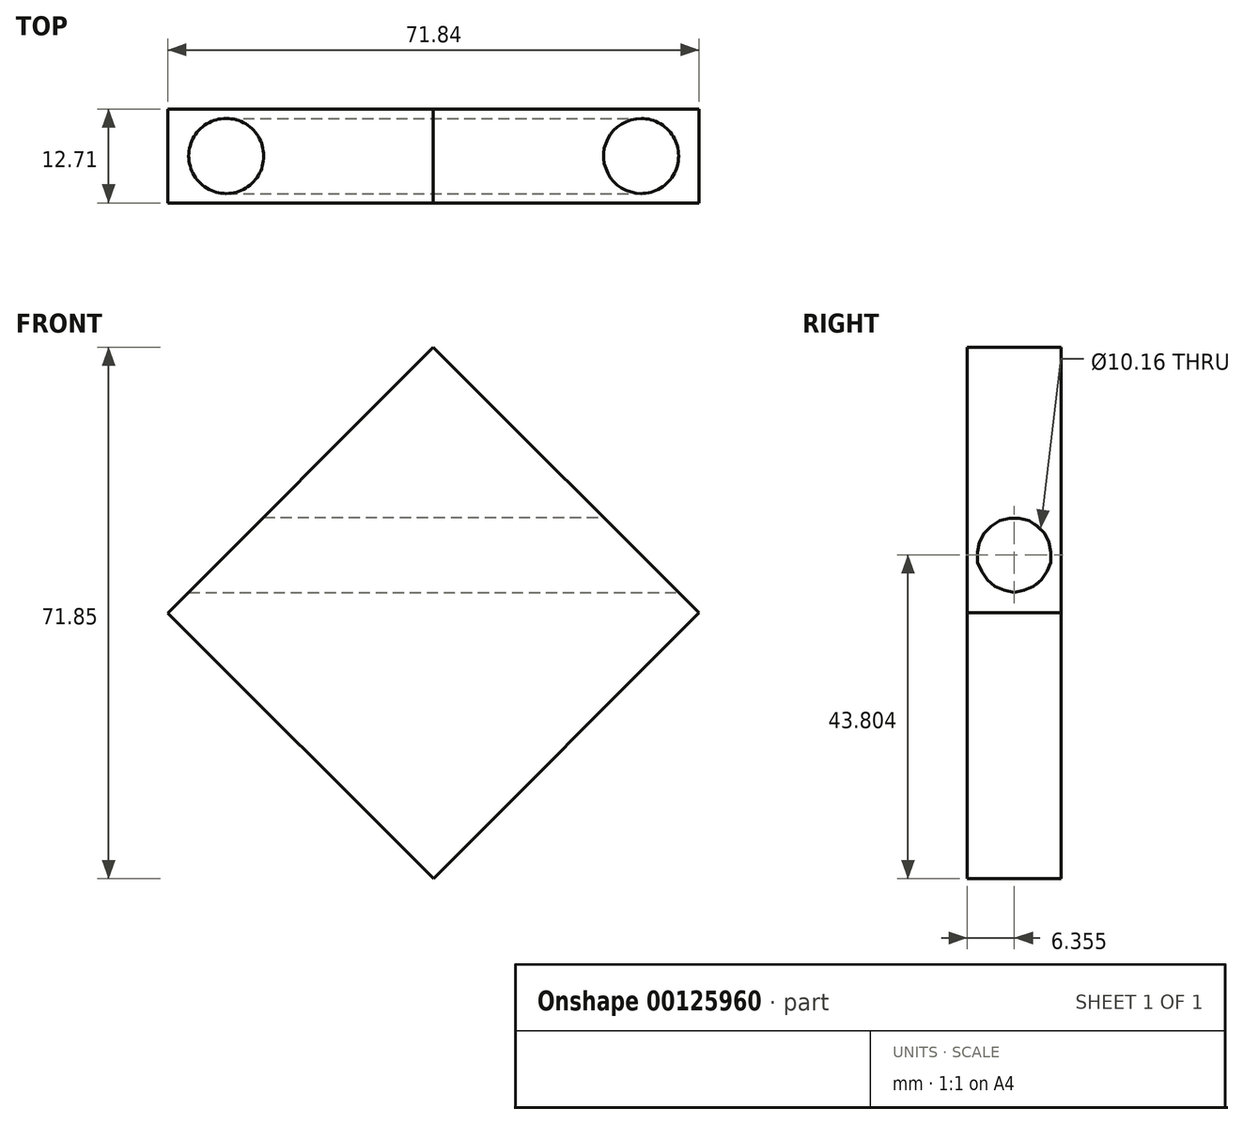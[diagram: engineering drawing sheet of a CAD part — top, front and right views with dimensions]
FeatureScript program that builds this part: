
annotation { "Feature Type Name" : "Feature", "Feature Type Description" : "" }
export const myFeature = defineFeature(function(context is Context, id is Id, definition is map)
    precondition{}
    {
        {
            var Q0;
            Q0=qCreatedBy(makeId("Front.planeOp"),FACE);
            var sketch = newSketch(context, id + "F0", { "sketchPlane" : qUnion([Q0])});
            skLineSegment(sketch, "E0.bottom", {"start": v(-99.41, 44.45) * mm, "end": v(103.79, 44.45) * mm});
            skLineSegment(sketch, "E0.top", {"start": v(-99.41, 0) * mm, "end": v(103.79, 0) * mm});
            skLineSegment(sketch, "E0.left", {"start": v(-99.41, 44.45) * mm, "end": v(-99.41, 0) * mm});
            skLineSegment(sketch, "E0.right", {"start": v(103.79, 44.45) * mm, "end": v(103.79, 0) * mm});
            skSolve(sketch);
        }
        {
            var Q0;
            Q0 = qSketchRegion(id + "F0", true);
            extrude(context, id + "F1", {"entities" : qUnion([Q0]), "endBound" : BoundingType.SYMMETRIC, "depth" : 6.35 * mm});
        }
        {
            var Q0;
            Q0=makeQuery(id+"F1.opExtrude","CAP_FACE",FACE,{"disambiguationData":[OSD([sQuery(id+"F0.wireOp",EDGE,"E0.bottom"),sQuery(id+"F0.wireOp",EDGE,"E0.top"),sQuery(id+"F0.wireOp",EDGE,"E0.left"),sQuery(id+"F0.wireOp",EDGE,"E0.right")])],"isStart":false});
            var sketch = newSketch(context, id + "F2", { "sketchPlane" : qUnion([Q0])});
            skLineSegment(sketch, "E1.bottom", {"start": v(38.1, 22.25) * mm, "end": v(2.16, 58.15) * mm});
            skLineSegment(sketch, "E1.top", {"start": v(2.21, -13.7) * mm, "end": v(-33.73, 22.2) * mm});
            skLineSegment(sketch, "E1.left", {"start": v(38.1, 22.25) * mm, "end": v(2.21, -13.7) * mm});
            skLineSegment(sketch, "E1.right", {"start": v(2.16, 58.15) * mm, "end": v(-33.73, 22.2) * mm});
            skPoint(sketch, "E1.middle", {"position": v(2.19, 22.23) * mm});
            skSolve(sketch);
        }
        {
            var Q0;
            Q0 = qSketchRegion(id + "F2", true);
            extrude(context, id + "F3", {"entities" : qUnion([Q0]), "operationType" : NewBodyOperationType.ADD, "endBound" : BoundingType.SYMMETRIC, "depth" : 12.7 * mm});
        }
        {
            var Q0;
            Q0=makeQuery(id+"F1.opExtrude","SWEPT_BODY",BODY,{"disambiguationData":[OSD([sQuery(id+"F0.wireOp",EDGE,"E0.bottom"),sQuery(id+"F0.wireOp",EDGE,"E0.top"),sQuery(id+"F0.wireOp",EDGE,"E0.left"),sQuery(id+"F0.wireOp",EDGE,"E0.right")])]});
            transform(context, id + "F4", {"entities" : qUnion([Q0]), "transformType" : TransformType.TRANSLATION_3D, "dx" : -2.2 * mm, "dy" : 0 * mm, "dz" : 0 * mm, "makeCopy" : false});
        }
        {
            var Q0;
            {var subQ0=sQuery(id+"F0.wireOp",EDGE,"E0.left");var subQ1=sQuery(id+"F0.wireOp",EDGE,"E0.top");var subQ2=sQuery(id+"F0.wireOp",EDGE,"E0.bottom");Q0=makeQuery(id+"F3.boolean.opBoolean","SPLIT",FACE,{"disambiguationData":[TD([makeQuery(id+"F1.opExtrude","SWEPT_FACE",FACE,{"disambiguationData":[OSD([subQ0])]})])],"derivedFrom":makeQuery(id+"F1.opExtrude","CAP_FACE",FACE,{"disambiguationData":[OSD([subQ2,subQ1,subQ0,sQuery(id+"F0.wireOp",EDGE,"E0.right")])],"isStart":false})});}
            extrude(context, id + "F5", {"entities" : qUnion([Q0]), "operationType" : NewBodyOperationType.REMOVE, "oppositeDirection" : true, "depth" : 25.4 * mm});
        }
        {
            var Q0;
            {var subQ0=sQuery(id+"F0.wireOp",EDGE,"E0.right");var subQ1=sQuery(id+"F0.wireOp",EDGE,"E0.top");var subQ2=sQuery(id+"F0.wireOp",EDGE,"E0.bottom");Q0=makeQuery(id+"F3.boolean.opBoolean","SPLIT",FACE,{"disambiguationData":[TD([makeQuery(id+"F1.opExtrude","SWEPT_FACE",FACE,{"disambiguationData":[OSD([subQ0])]})])],"derivedFrom":makeQuery(id+"F1.opExtrude","CAP_FACE",FACE,{"disambiguationData":[OSD([subQ2,subQ1,sQuery(id+"F0.wireOp",EDGE,"E0.left"),subQ0])],"isStart":false})});}
            extrude(context, id + "F6", {"entities" : qUnion([Q0]), "operationType" : NewBodyOperationType.REMOVE, "oppositeDirection" : true, "depth" : 25.4 * mm});
        }
        {
            var Q0;
            Q0=makeQuery(id+"F3.opExtrude","CAP_FACE",FACE,{"disambiguationData":[OSD([sQuery(id+"F2.wireOp",EDGE,"E1.bottom"),sQuery(id+"F2.wireOp",EDGE,"E1.top"),sQuery(id+"F2.wireOp",EDGE,"E1.left"),sQuery(id+"F2.wireOp",EDGE,"E1.right")])],"isStart":false});
            var sketch = newSketch(context, id + "F7", { "sketchPlane" : qUnion([Q0])});
            skLineSegment(sketch, "E2", {"start": v(-0.04, 58.15) * mm, "end": v(35.9, 58.15) * mm});
            skLineSegment(sketch, "E3", {"start": v(35.9, 22.25) * mm, "end": v(35.9, 58.15) * mm});
            skLineSegment(sketch, "E4", {"start": v(-35.94, 22.2) * mm, "end": v(-35.94, 58.15) * mm});
            skLineSegment(sketch, "E5", {"start": v(-35.94, 58.15) * mm, "end": v(-0.04, 58.15) * mm});
            skSolve(sketch);
        }
        {
            var Q0;
            Q0=makeQuery(id+"F7.imprint","IMPRINT",FACE,{"disambiguationData":[TD([[makeQuery(id+"F7.imprint","IMPRINT",EDGE,{"derivedFrom":sQuery(id+"F7.wireOp",EDGE,"E2")}),-1.0]])]});
            var Q1;
            Q1=makeQuery(id+"F7.imprint","IMPRINT",FACE,{"disambiguationData":[TD([[makeQuery(id+"F7.imprint","IMPRINT",EDGE,{"derivedFrom":sQuery(id+"F7.wireOp",EDGE,"E4")}),-1.0]])]});
            extrude(context, id + "F8", {"entities" : qUnion([Q0, Q1]), "operationType" : NewBodyOperationType.ADD, "oppositeDirection" : true, "depth" : 12.7 * mm});
        }
        {
            var Q0;
            Q0=makeQuery(id+"F8.opExtrude","SWEPT_FACE",FACE,{"disambiguationData":[OSD([sQuery(id+"F7.wireOp",EDGE,"E3")])]});
            var sketch = newSketch(context, id + "F9", { "sketchPlane" : qUnion([Q0])});
            skCircle(sketch, "E6", {"center": v(-3.17, 30.1) * mm, "radius": 5.08 * mm});
            skPoint(sketch, "E6.centerSnap0", {"position": v(-3.17, 58.15) * mm});
            skSolve(sketch);
        }
        {
            var Q0;
            Q0=makeQuery(id+"F9.imprint","IMPRINT",FACE,{"disambiguationData":[TD([[makeQuery(id+"F9.imprint","IMPRINT",EDGE,{"derivedFrom":sQuery(id+"F9.wireOp",EDGE,"E6")}),1.0]])]});
            extrude(context, id + "F10", {"entities" : qUnion([Q0]), "operationType" : NewBodyOperationType.REMOVE, "oppositeDirection" : true, "depth" : 76.2 * mm});
        }
        {
            var Q0;
            {var subQ0=sQuery(id+"F2.wireOp",EDGE,"E1.right");var subQ1=sQuery(id+"F2.wireOp",EDGE,"E1.bottom");Q0=makeQuery(id+"F8.boolean.opBoolean","MERGE",FACE,{"derivedFrom":[makeQuery(id+"F3.opExtrude","CAP_FACE",FACE,{"disambiguationData":[OSD([subQ1,sQuery(id+"F2.wireOp",EDGE,"E1.top"),sQuery(id+"F2.wireOp",EDGE,"E1.left"),subQ0])],"isStart":false}),makeQuery(id+"F8.opExtrude","CAP_FACE",FACE,{"disambiguationData":[OSD([subQ1,sQuery(id+"F7.wireOp",EDGE,"E2"),sQuery(id+"F7.wireOp",EDGE,"E3")])],"isStart":true}),makeQuery(id+"F8.opExtrude","CAP_FACE",FACE,{"disambiguationData":[OSD([subQ0,sQuery(id+"F7.wireOp",EDGE,"E4"),sQuery(id+"F7.wireOp",EDGE,"E5")])],"isStart":true})]});}
            var sketch = newSketch(context, id + "F11", { "sketchPlane" : qUnion([Q0])});
            skLineSegment(sketch, "E7", {"start": v(-35.94, 22.2) * mm, "end": v(-0.04, 58.15) * mm});
            skLineSegment(sketch, "E8", {"start": v(-0.04, 58.15) * mm, "end": v(35.9, 22.25) * mm});
            skSolve(sketch);
        }
        {
            var Q0;
            {var subQ0=sQuery(id+"F11.wireOp",EDGE,"E8");Q0=makeQuery(id+"F11.imprint","IMPRINT",FACE,{"disambiguationData":[TD([[makeQuery(id+"F11.imprint","IMPRINT",EDGE,{"derivedFrom":subQ0}),1.0]])]});}
            var Q1;
            {var subQ0=sQuery(id+"F11.wireOp",EDGE,"E7");Q1=makeQuery(id+"F11.imprint","IMPRINT",FACE,{"disambiguationData":[TD([[makeQuery(id+"F11.imprint","IMPRINT",EDGE,{"derivedFrom":subQ0}),1.0]])]});}
            extrude(context, id + "F12", {"entities" : qUnion([Q0, Q1]), "operationType" : NewBodyOperationType.REMOVE, "oppositeDirection" : true, "depth" : 25.4 * mm});
        }
    });
